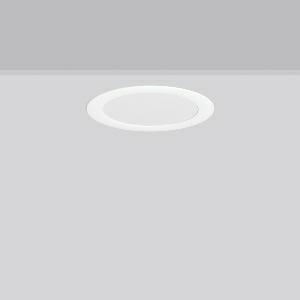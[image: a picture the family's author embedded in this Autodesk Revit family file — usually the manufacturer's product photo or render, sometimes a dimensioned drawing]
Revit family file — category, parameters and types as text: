
# Revit family: toledo_flat_round_e_672230_002_3806
name_source: partatom
category: Lighting Fixtures
units: mm (PartAtom-declared; Revit-internal decimal feet)

## family parameters
Cut with Voids When Loaded = No
Host = Face
Light Source = No
Part Type = Normal
Room Calculation Point = No
Round Connector Dimension = Use Diameter
Shared = No

## types (1)
- TOLEDO FLAT round E (1 x LED Modul 830, 1650 lm, 3000)
    Apparent Load = 17 VA
    CIE Flux Codes = 48 79 96 100 100
    Color Rendering = 80
    Color Temperature = 3000
    Default Elevation = 1800 mm
    Description = Series: TOLEDO FLAT round
Ultra thin recessed downlight. For escape route illumination. Housing: die-cast aluminium, powder-coated. Lightguide and diffuser made of non-yellowing plastic (PMMA). Diffuser opal matt plastic. Ceiling installation with spring system. Including separate LED converter with connecting cable 250 mm. Suitable for connection to central battery systems. External driver with simple plug-in locking system. 
Colour: white
Diameter: 255 mm
Height: 3 mm
Cut-out diameter: 234 mm
Recess height: 35 mm
Luminaire: recess height: 31-51 mm
Weight: 0.81 kg
Operating mode: maintained power mode
Lamp: LED
Socket: without socket
Colour temperature: 3000K
Colour rendering index (CRI): 80
System power: 17 W
Rated luminous flux: 1650 lm
Luminous flux, emergency: 1650 lm
System power, emergency: 17 W
Control gear: Regulated power supply
Protection class: II
Type of protection: IP 54
    Height = 0 mm  [stored 0 ft]
    Lamp = 1 x LED Modul 830
    Lamp Light Flux = 1650 lm
    Lamp count = 1
    Length = 255 mm
    Lifetime = 50000 h
    Luminous efficacy = 97 lm/W
    Manufacturer = RZB
    ModVariant = No
    Model = 672230.002
    Mounting Place = Ceiling
    Mounting Type = Recessed
    Number of Poles = 1
    OnlyDefault = Yes
    Power Factor = 1
    Product Name = TOLEDO FLAT round E
    Product group = Recessed downlights
    ProductGroupID = 402
    Protection Class = Protection class II
    Protection Degree = IP 40
    RLX_Detail_Level = 1
    RLX_Emergency_Light_Flux = 1650 lm
    RLX_Emergency_Type = 3
    RLX_Emergency_Type_DB = Yes
    RlxData = <blob elided: 29845 chars, md5=2c87f402>
    Socket = socket
    Standby Power = 0 W
    System Light Flux = 1650 lm
    System Power = 17 W
    Type Comments = Product without accessories
    Type Image = 901453.002.jpg
    URL = http://relux.com
    VarID = ---
    Voltage = 230 V
    Voltage Range = 220-240 V
    Weight = 0.00 kg
    Width = 0 mm  [stored 0 ft]

note: [stored X ft] marks values corroborated as IEEE doubles in the binary element streams (Revit-internal decimal feet)

## geometry (parser evidence)
native form markers: Blend x4, Sweep x9
no freeform markers — native parametric forms only
